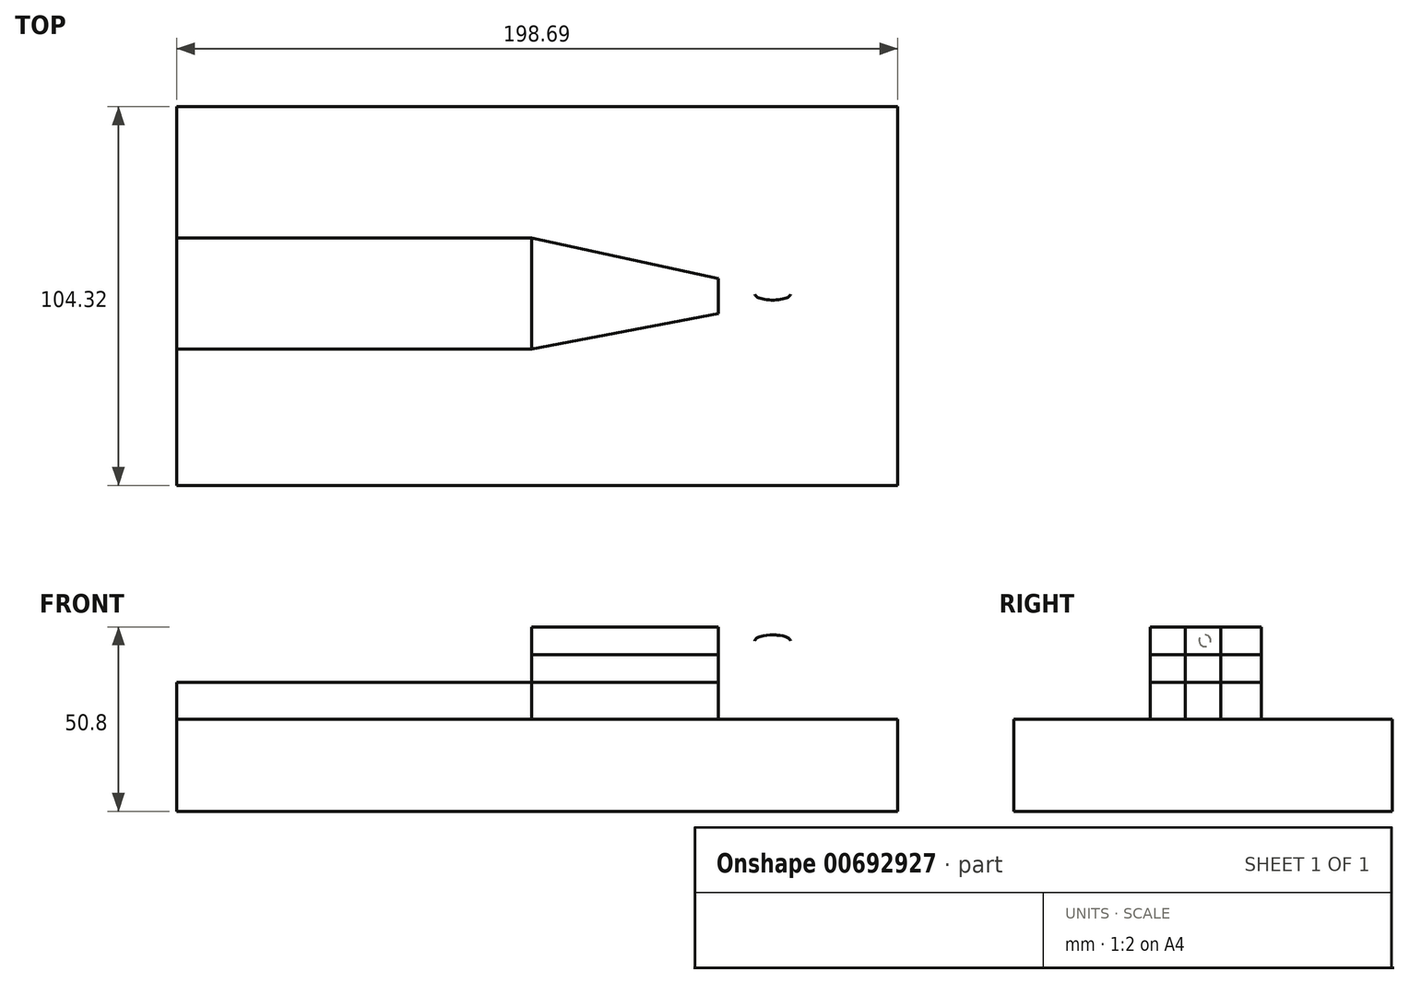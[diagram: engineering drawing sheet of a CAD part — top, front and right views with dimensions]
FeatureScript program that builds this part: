
annotation { "Feature Type Name" : "Feature", "Feature Type Description" : "" }
export const myFeature = defineFeature(function(context is Context, id is Id, definition is map)
    precondition{}
    {
        {
            var Q0;
            Q0=qCreatedBy(makeId("Top.planeOp"),FACE);
            var sketch = newSketch(context, id + "F0", { "sketchPlane" : qUnion([Q0])});
            skLineSegment(sketch, "E0.left", {"start": v(-149.3, 52.16) * mm, "end": v(-149.3, -52.16) * mm});
            skPoint(sketch, "E0.middle", {"position": v(0, 0) * mm});
            skLineSegment(sketch, "E1", {"start": v(-149.3, 52.16) * mm, "end": v(49.39, 52.16) * mm});
            skLineSegment(sketch, "E2", {"start": v(49.39, 52.16) * mm, "end": v(49.39, -52.16) * mm});
            skLineSegment(sketch, "E3", {"start": v(49.39, -52.16) * mm, "end": v(-149.3, -52.16) * mm});
            skSolve(sketch);
        }
        {
            var Q0;
            Q0=qSketchRegion(id+"F0",true);
            var Q1;
            Q1=makeQuery(id+"F0.imprint","IMPRINT",FACE,{"disambiguationData":[TD([[makeQuery(id+"F0.imprint","IMPRINT",EDGE,{"derivedFrom":sQuery(id+"F0.wireOp",EDGE,"E0.bottom")}),-1.0]])]});
            extrude(context, id + "F1", {"entities" : qUnion([Q0, Q1]), "oppositeDirection" : true, "depth" : 25.4 * mm, "offsetDistance" : 25.4 * mm});
        }
        {
            var Q0;
            Q0=makeQuery(id+"F1.opExtrude","CAP_FACE",FACE,{"disambiguationData":[OSD([sQuery(id+"F0.wireOp",EDGE,"E0.bottom"),sQuery(id+"F0.wireOp",EDGE,"E0.top"),sQuery(id+"F0.wireOp",EDGE,"E0.left"),sQuery(id+"F0.wireOp",EDGE,"E0.right")])],"isStart":true});
            var sketch = newSketch(context, id + "F2", { "sketchPlane" : qUnion([Q0])});
            skLineSegment(sketch, "E4", {"start": v(-51.41, 16.02) * mm, "end": v(0, 4.87) * mm});
            skLineSegment(sketch, "E5", {"start": v(0, 4.87) * mm, "end": v(0, -4.87) * mm});
            skLineSegment(sketch, "E6", {"start": v(0, -4.87) * mm, "end": v(-51.41, -14.6) * mm});
            skLineSegment(sketch, "E7", {"start": v(-51.41, 16.02) * mm, "end": v(-149.21, 16.02) * mm});
            skLineSegment(sketch, "E8", {"start": v(-149.21, 16.02) * mm, "end": v(-149.21, -14.6) * mm});
            skLineSegment(sketch, "E9", {"start": v(-149.21, -14.6) * mm, "end": v(-51.41, -14.6) * mm});
            skSolve(sketch);
        }
        {
            var Q0;
            Q0=qSketchRegion(id+"F2",true);
            extrude(context, id + "F3", {"entities" : qUnion([Q0]), "depth" : 10.16 * mm, "offsetDistance" : 25.4 * mm});
        }
        {
            var Q0;
            Q0=makeQuery(id+"F3.opExtrude","CAP_FACE",FACE,{"disambiguationData":[OSD([sQuery(id+"F2.wireOp",EDGE,"E4"),sQuery(id+"F2.wireOp",EDGE,"E5"),sQuery(id+"F2.wireOp",EDGE,"E6"),sQuery(id+"F2.wireOp",EDGE,"E7"),sQuery(id+"F2.wireOp",EDGE,"E8"),sQuery(id+"F2.wireOp",EDGE,"E9")])],"isStart":false});
            var sketch = newSketch(context, id + "F4", { "sketchPlane" : qUnion([Q0])});
            skLineSegment(sketch, "E10", {"start": v(-51.41, 16.02) * mm, "end": v(0, 4.87) * mm});
            skLineSegment(sketch, "E11", {"start": v(0, 4.87) * mm, "end": v(0, -4.87) * mm});
            skLineSegment(sketch, "E12", {"start": v(0, -4.87) * mm, "end": v(-51.41, -14.6) * mm});
            skLineSegment(sketch, "E13", {"start": v(-51.41, -14.6) * mm, "end": v(-51.41, 16.02) * mm});
            skSolve(sketch);
        }
        {
            var Q0;
            Q0=qSketchRegion(id+"F4",true);
            extrude(context, id + "F5", {"entities" : qUnion([Q0]), "depth" : 7.62 * mm, "offsetDistance" : 25.4 * mm});
        }
        {
            var Q0;
            Q0=makeQuery(id+"F5.opExtrude","CAP_FACE",FACE,{"disambiguationData":[OSD([sQuery(id+"F4.wireOp",EDGE,"E10"),sQuery(id+"F4.wireOp",EDGE,"E11"),sQuery(id+"F4.wireOp",EDGE,"E12"),sQuery(id+"F4.wireOp",EDGE,"E13")])],"isStart":false});
            var sketch = newSketch(context, id + "F6", { "sketchPlane" : qUnion([Q0])});
            skLineSegment(sketch, "E14", {"start": v(-51.41, 16.02) * mm, "end": v(0, 4.87) * mm});
            skLineSegment(sketch, "E15", {"start": v(0, 4.87) * mm, "end": v(0, -4.87) * mm});
            skLineSegment(sketch, "E16", {"start": v(0, -4.87) * mm, "end": v(-51.41, -14.6) * mm});
            skLineSegment(sketch, "E17", {"start": v(-51.41, -14.6) * mm, "end": v(-51.41, 16.02) * mm});
            skSolve(sketch);
        }
        {
            var Q0;
            Q0=qSketchRegion(id+"F6",true);
            extrude(context, id + "F7", {"entities" : qUnion([Q0]), "depth" : 7.62 * mm, "offsetDistance" : 25.4 * mm});
        }
        {
            var Q0;
            Q0=makeQuery(id+"F7.opExtrude","CAP_FACE",FACE,{"disambiguationData":[OSD([sQuery(id+"F6.wireOp",EDGE,"E14"),sQuery(id+"F6.wireOp",EDGE,"E15"),sQuery(id+"F6.wireOp",EDGE,"E16"),sQuery(id+"F6.wireOp",EDGE,"E17")])],"isStart":false});
            cPlane(context, id + "F8", {"entities" : qUnion([Q0]), "cplaneType" : CPlaneType.OFFSET, "offset" : 3.8 * mm, "oppositeDirection" : true, "width" : 152.4 * mm, "height" : 152.4 * mm});
        }
        {
            var Q0;
            Q0=qCreatedBy(id+"F8.planeOp",FACE);
            var sketch = newSketch(context, id + "F9", { "sketchPlane" : qUnion([Q0])});
            skEllipse(sketch, "E18", {"center": v(14.96, 0.56) * mm, "majorRadius": 4.93 * mm, "minorRadius": 1.67 * mm, "majorAxis": v(-1, 0)});
            skLineSegment(sketch, "E19", {"start": v(7.92, 0.5) * mm, "end": v(23.83, 0.5) * mm});
            skSolve(sketch);
        }
        {
            var Q0;
            {var subQ0=sQuery(id+"F9.wireOp",EDGE,"E19");var subQ1=sQuery(id+"F9.wireOp",EDGE,"E18");var subQ2=makeQuery(id+"F9.imprint","INTERSECT",VERTEX,{"disambiguationData":[OD(0.0)],"derivedFrom":[subQ1,subQ0]});Q0=makeQuery(id+"F9.imprint","IMPRINT",FACE,{"disambiguationData":[TD([[makeQuery(id+"F9.imprint","IMPRINT",EDGE,{"disambiguationData":[TD([[subQ2,1.0]])],"derivedFrom":subQ1}),1.0]])]});}
            var Q1;
            Q1=sQuery(id+"F9.wireOp",EDGE,"E18");
            var Q2;
            Q2=sQuery(id+"F9.wireOp",EDGE,"E19");
            revolve(context, id + "F10", {"surfaceOperationType" : NewSurfaceOperationType.NEW, "entities" : qUnion([Q0]), "surfaceEntities" : qUnion([Q1]), "axis" : qUnion([Q2]), "revolveType" : RevolveType.FULL});
        }
    });
